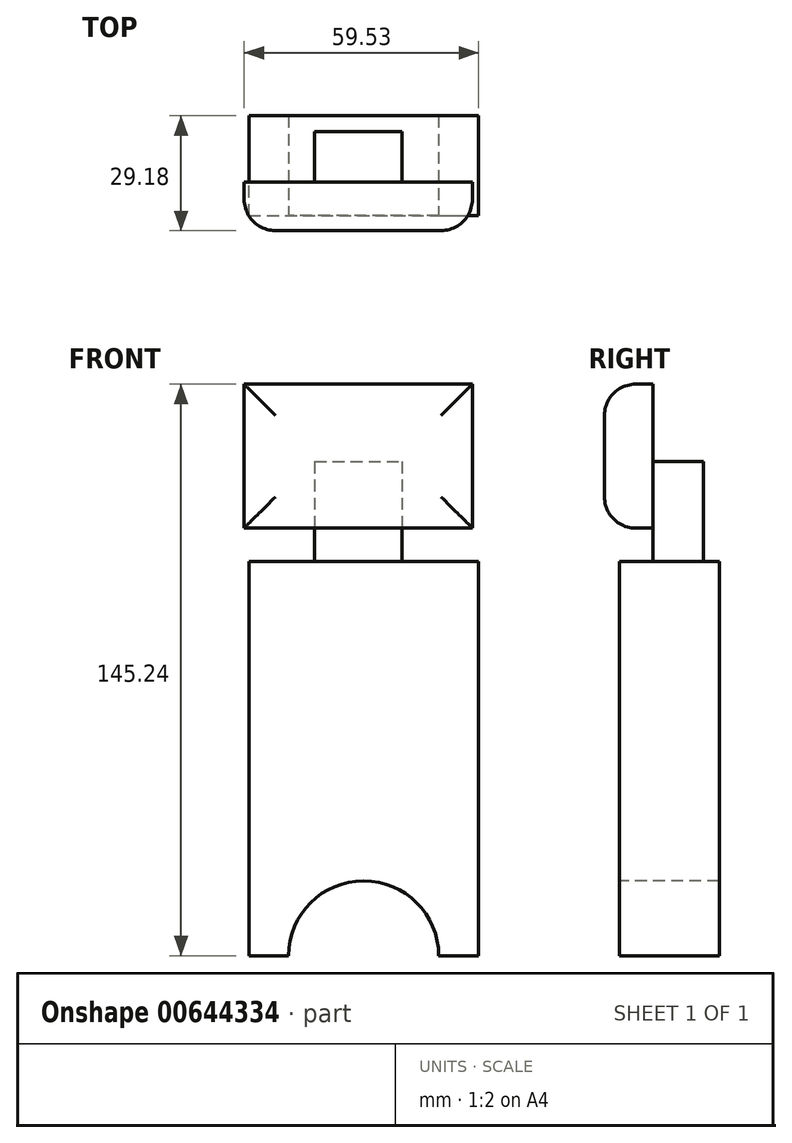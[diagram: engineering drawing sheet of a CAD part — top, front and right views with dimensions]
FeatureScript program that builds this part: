
annotation { "Feature Type Name" : "Feature", "Feature Type Description" : "" }
export const myFeature = defineFeature(function(context is Context, id is Id, definition is map)
    precondition{}
    {
        {
            var Q0;
            Q0=qCreatedBy(makeId("Front.planeOp"),FACE);
            var sketch = newSketch(context, id + "F0", { "sketchPlane" : qUnion([Q0])});
            skLineSegment(sketch, "E0.bottom", {"start": v(-28.93, -41.8) * mm, "end": v(29.4, -41.8) * mm});
            skLineSegment(sketch, "E0.top", {"start": v(-28.93, 58.37) * mm, "end": v(29.4, 58.37) * mm});
            skLineSegment(sketch, "E0.left", {"start": v(-28.93, -41.8) * mm, "end": v(-28.93, 58.37) * mm});
            skLineSegment(sketch, "E0.right", {"start": v(29.4, -41.8) * mm, "end": v(29.4, 58.37) * mm});
            skPoint(sketch, "E0.middle", {"position": v(0.23, 8.29) * mm});
            skSolve(sketch);
        }
        {
            var Q0;
            Q0 = qSketchRegion(id + "F0", true);
            extrude(context, id + "F1", {"entities" : qUnion([Q0]), "depth" : 25.4 * mm, "offsetDistance" : 25.4 * mm});
        }
        {
            var Q0;
            Q0=makeQuery(id+"F1.opExtrude","CAP_FACE",FACE,{"disambiguationData":[OSD([sQuery(id+"F0.wireOp",EDGE,"E0.bottom"),sQuery(id+"F0.wireOp",EDGE,"E0.top"),sQuery(id+"F0.wireOp",EDGE,"E0.left"),sQuery(id+"F0.wireOp",EDGE,"E0.right")])],"isStart":false});
            var sketch = newSketch(context, id + "F2", { "sketchPlane" : qUnion([Q0])});
            skCircle(sketch, "E1", {"center": v(0.23, -41.8) * mm, "radius": 17.81 * mm});
            skSolve(sketch);
        }
        {
            var Q0;
            Q0=sQuery(id+"F2.wireOp",VERTEX,"E1.center");
            var Q1;
            Q1=makeQuery(id+"F1.opExtrude","SWEPT_BODY",BODY,{"disambiguationData":[OSD([sQuery(id+"F0.wireOp",EDGE,"E0.bottom"),sQuery(id+"F0.wireOp",EDGE,"E0.top"),sQuery(id+"F0.wireOp",EDGE,"E0.left"),sQuery(id+"F0.wireOp",EDGE,"E0.right")])]});
            hole(context, id + "F3", {"style" : HoleStyle.SIMPLE, "endStyle" : HoleEndStyle.THROUGH, "holeDiameter" : 38.1 * mm, "majorDiameter" : 6.35 * mm, "isTappedThrough" : true, "tappedDepth" : 12.7 * mm, "tapClearance" : 3, "locations" : qUnion([Q0]), "scope" : qUnion([Q1])});
        }
        {
            var Q0;
            Q0=makeQuery(id+"F1.opExtrude","SWEPT_FACE",FACE,{"disambiguationData":[OSD([sQuery(id+"F0.wireOp",EDGE,"E0.top")])]});
            var sketch = newSketch(context, id + "F4", { "sketchPlane" : qUnion([Q0])});
            skSolve(sketch);
        }
        {
            var Q0;
            {var subQ0=sQuery(id+"F0.wireOp",EDGE,"E0.top");Q0=makeQuery(id+"F4.imprint","IMPRINT",FACE,{"disambiguationData":[TD([[makeQuery(id+"F4.imprint","IMPRINT",EDGE,{"derivedFrom":makeQuery(id+"F1.opExtrude","CAP_EDGE",EDGE,{"disambiguationData":[OSD([subQ0])],"isStart":true})}),-1.0]])]});}
            var sketch = newSketch(context, id + "F5", { "sketchPlane" : qUnion([Q0])});
            skLineSegment(sketch, "E2.bottom", {"start": v(-12.26, -16.9) * mm, "end": v(10.03, -16.9) * mm});
            skLineSegment(sketch, "E2.top", {"start": v(-12.26, -3.96) * mm, "end": v(10.03, -3.96) * mm});
            skLineSegment(sketch, "E2.left", {"start": v(-12.26, -16.9) * mm, "end": v(-12.26, -3.96) * mm});
            skLineSegment(sketch, "E2.right", {"start": v(10.03, -16.9) * mm, "end": v(10.03, -3.96) * mm});
            skPoint(sketch, "E2.middle", {"position": v(-1.12, -10.43) * mm});
            skSolve(sketch);
        }
        {
            var Q0;
            Q0 = qSketchRegion(id + "F5", true);
            extrude(context, id + "F6", {"entities" : qUnion([Q0]), "operationType" : NewBodyOperationType.ADD, "depth" : 25.4 * mm, "offsetDistance" : 25.4 * mm});
        }
        {
            var Q0;
            Q0=makeQuery(id+"F6.opExtrude","SWEPT_FACE",FACE,{"disambiguationData":[OSD([sQuery(id+"F5.wireOp",EDGE,"E2.bottom")])]});
            var sketch = newSketch(context, id + "F7", { "sketchPlane" : qUnion([Q0])});
            skSolve(sketch);
        }
        {
            var Q0;
            {var subQ0=sQuery(id+"F5.wireOp",EDGE,"E2.bottom");Q0=makeQuery(id+"F7.imprint","IMPRINT",FACE,{"disambiguationData":[TD([[makeQuery(id+"F7.imprint","IMPRINT",EDGE,{"derivedFrom":makeQuery(id+"F6.opExtrude","CAP_EDGE",EDGE,{"disambiguationData":[OSD([subQ0])],"isStart":false})}),-1.0]])]});}
            var sketch = newSketch(context, id + "F8", { "sketchPlane" : qUnion([Q0])});
            skLineSegment(sketch, "E3.bottom", {"start": v(-30.13, 66.85) * mm, "end": v(27.86, 66.85) * mm});
            skLineSegment(sketch, "E3.top", {"start": v(-30.13, 103.45) * mm, "end": v(27.86, 103.45) * mm});
            skLineSegment(sketch, "E3.left", {"start": v(-30.13, 66.85) * mm, "end": v(-30.13, 103.45) * mm});
            skLineSegment(sketch, "E3.right", {"start": v(27.86, 66.85) * mm, "end": v(27.86, 103.45) * mm});
            skPoint(sketch, "E3.middle", {"position": v(-1.13, 85.15) * mm});
            skSolve(sketch);
        }
        {
            var Q0;
            Q0 = qSketchRegion(id + "F8", true);
            extrude(context, id + "F9", {"entities" : qUnion([Q0]), "operationType" : NewBodyOperationType.ADD, "depth" : 12.29 * mm, "offsetDistance" : 25.4 * mm});
        }
        {
            var Q0;
            Q0=makeQuery(id+"F9.opExtrude","CAP_EDGE",EDGE,{"disambiguationData":[OSD([sQuery(id+"F8.wireOp",EDGE,"E3.right")])],"isStart":false});
            var Q1;
            Q1=makeQuery(id+"F9.opExtrude","CAP_EDGE",EDGE,{"disambiguationData":[OSD([sQuery(id+"F8.wireOp",EDGE,"E3.top")])],"isStart":false});
            var Q2;
            Q2=makeQuery(id+"F9.opExtrude","CAP_EDGE",EDGE,{"disambiguationData":[OSD([sQuery(id+"F8.wireOp",EDGE,"E3.bottom")])],"isStart":false});
            var Q3;
            Q3=makeQuery(id+"F9.opExtrude","CAP_EDGE",EDGE,{"disambiguationData":[OSD([sQuery(id+"F8.wireOp",EDGE,"E3.left")])],"isStart":false});
            fillet(context, id + "F10", {"entities" : qUnion([Q0, Q1, Q2, Q3]), "radius" : 7.93 * mm, "tangentPropagation" : true, "allowEdgeOverflow" : false});
        }
    });
